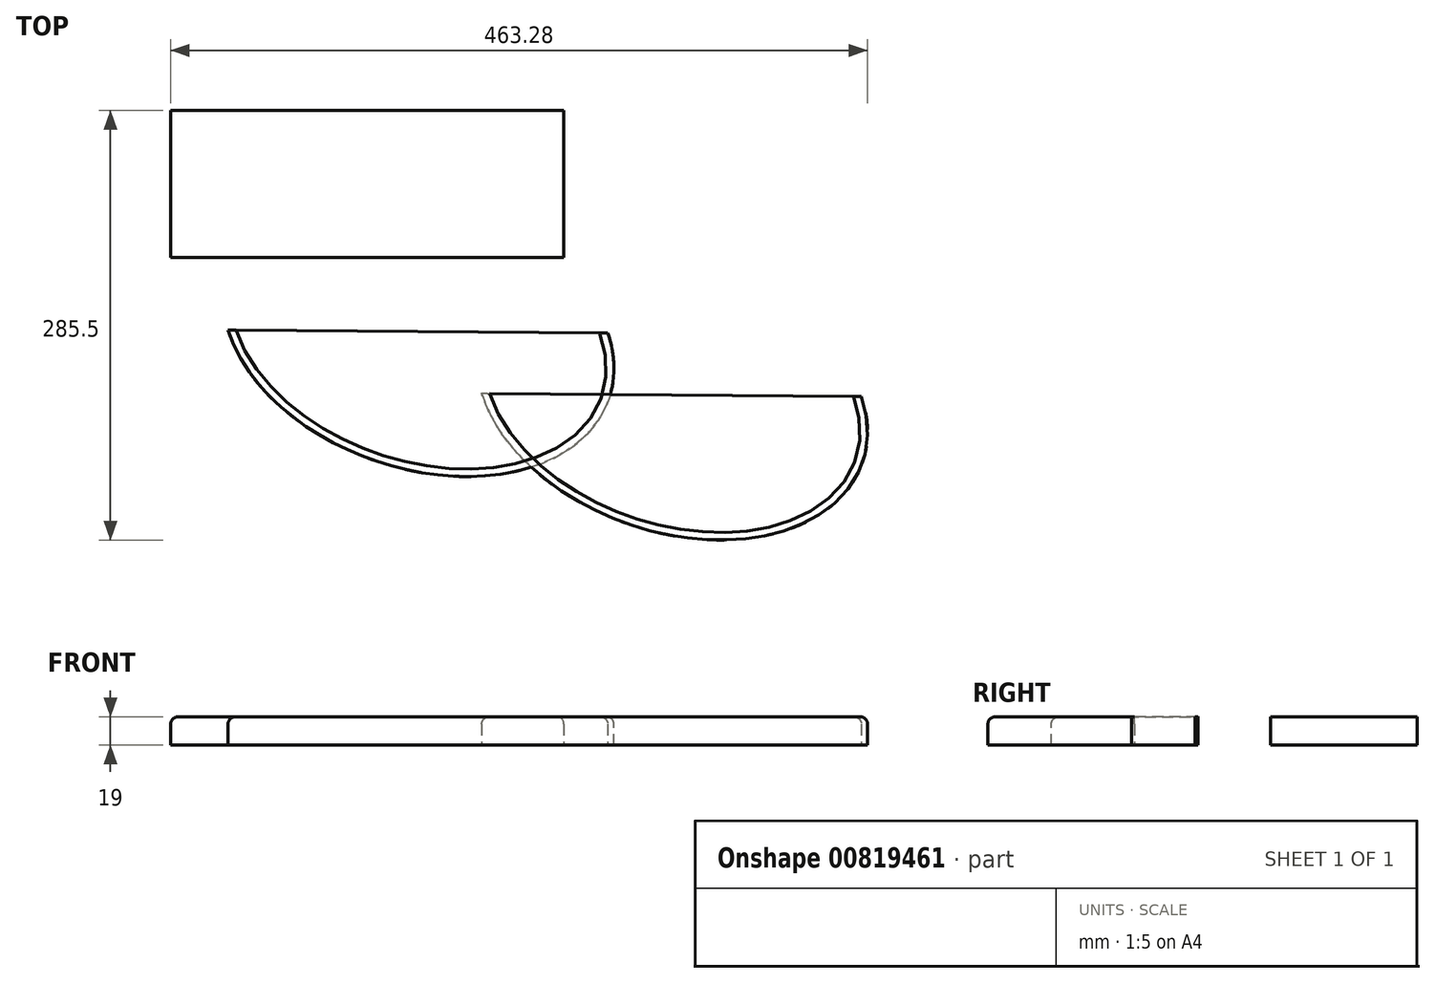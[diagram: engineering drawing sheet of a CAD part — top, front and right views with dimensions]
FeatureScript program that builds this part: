
annotation { "Feature Type Name" : "Feature", "Feature Type Description" : "" }
export const myFeature = defineFeature(function(context is Context, id is Id, definition is map)
    precondition{}
    {
        {
            var Q0;
            Q0=qCreatedBy(makeId("Top.planeOp"),FACE);
            var sketch = newSketch(context, id + "F0", { "sketchPlane" : qUnion([Q0])});
            skEllipticalArc(sketch, "E0", {});
            skLineSegment(sketch, "E1", {"start": v(-257.7, 50.14) * mm, "end": v(0, 48.04) * mm});
            skPoint(sketch, "E1.startSnap0", {"position": v(-257.7, 91.98) * mm});
            const initialGuessF0  = {"E0": [-0.131116583943367, 0.048040200024843216, 0.9446937862758901, -0.32795373175453124, 0.1339859159948464, 0.08966357570015461, 3.598125766920572, 0.478987855163428]};
            skSetInitialGuess(sketch, initialGuessF0);
            skSolve(sketch);
        }
        {
            var Q0;
            Q0=qCreatedBy(makeId("Top.planeOp"),FACE);
            var sketch = newSketch(context, id + "F1", { "sketchPlane" : qUnion([Q0])});
            skEllipticalArc(sketch, "E2", {});
            skLineSegment(sketch, "E3", {"start": v(-89.03, 7.97) * mm, "end": v(168.66, 5.87) * mm});
            skPoint(sketch, "E3.startSnap0", {"position": v(-89.03, 49.81) * mm});
            const initialGuessF1  = {"E2": [0.037541152049757526, 0.005872024713239887, 0.9446937862758901, -0.32795373175453124, 0.1339859159948464, 0.08966357570015461, 3.598125766920572, 0.478987855163428]};
            skSetInitialGuess(sketch, initialGuessF1);
            skSolve(sketch);
        }
        {
            var Q0;
            Q0=qCreatedBy(makeId("Top.planeOp"),FACE);
            var sketch = newSketch(context, id + "F2", { "sketchPlane" : qUnion([Q0])});
            skLineSegment(sketch, "E4.bottom", {"start": v(-295.79, 195.95) * mm, "end": v(-34.37, 195.95) * mm});
            skLineSegment(sketch, "E4.top", {"start": v(-295.79, 98.2) * mm, "end": v(-34.37, 98.2) * mm});
            skLineSegment(sketch, "E4.left", {"start": v(-295.79, 195.95) * mm, "end": v(-295.79, 98.2) * mm});
            skLineSegment(sketch, "E4.right", {"start": v(-34.37, 195.95) * mm, "end": v(-34.37, 98.2) * mm});
            skSolve(sketch);
        }
        {
            var Q0;
            {var subQ0=sQuery(id+"F1.wireOp",EDGE,"E2");Q0=makeQuery(id+"F1.imprint","IMPRINT",FACE,{"disambiguationData":[TD([[makeQuery(id+"F1.imprint","IMPRINT",EDGE,{"derivedFrom":subQ0}),1.0]])]});}
            var Q1;
            {var subQ0=sQuery(id+"F0.wireOp",EDGE,"E0");Q1=makeQuery(id+"F0.imprint","IMPRINT",FACE,{"disambiguationData":[TD([[makeQuery(id+"F0.imprint","IMPRINT",EDGE,{"derivedFrom":subQ0}),1.0]])]});}
            var Q2;
            Q2=makeQuery(id+"F2.imprint","IMPRINT",FACE,{"disambiguationData":[TD([[makeQuery(id+"F2.imprint","IMPRINT",EDGE,{"derivedFrom":sQuery(id+"F2.wireOp",EDGE,"E4.bottom")}),-1.0]])]});
            extrude(context, id + "F3", {"entities" : qUnion([Q0, Q1, Q2]), "depth" : 19 * mm, "offsetDistance" : 25.4 * mm});
        }
        {
            var Q0;
            Q0=makeQuery(id+"F3.opExtrude","CAP_EDGE",EDGE,{"disambiguationData":[OSD([sQuery(id+"F1.wireOp",EDGE,"E2")])],"isStart":false});
            var Q1;
            Q1=makeQuery(id+"F3.opExtrude","CAP_EDGE",EDGE,{"disambiguationData":[OSD([sQuery(id+"F0.wireOp",EDGE,"E0")])],"isStart":false});
            fillet(context, id + "F4", {"entities" : qUnion([Q0, Q1]), "radius" : 5 * mm, "tangentPropagation" : true, "allowEdgeOverflow" : false});
        }
        {
            var Q0;
            Q0=makeQuery(id+"F3.opExtrude","CAP_EDGE",EDGE,{"disambiguationData":[OSD([sQuery(id+"F2.wireOp",EDGE,"E4.right")])],"isStart":false});
            fillet(context, id + "F5", {"entities" : qUnion([Q0]), "radius" : 5 * mm, "tangentPropagation" : true, "allowEdgeOverflow" : false});
        }
        {
            var Q0;
            Q0=makeQuery(id+"F3.opExtrude","CAP_EDGE",EDGE,{"disambiguationData":[OSD([sQuery(id+"F2.wireOp",EDGE,"E4.left")])],"isStart":false});
            fillet(context, id + "F6", {"entities" : qUnion([Q0]), "radius" : 5 * mm, "tangentPropagation" : true, "allowEdgeOverflow" : false});
        }
    });
